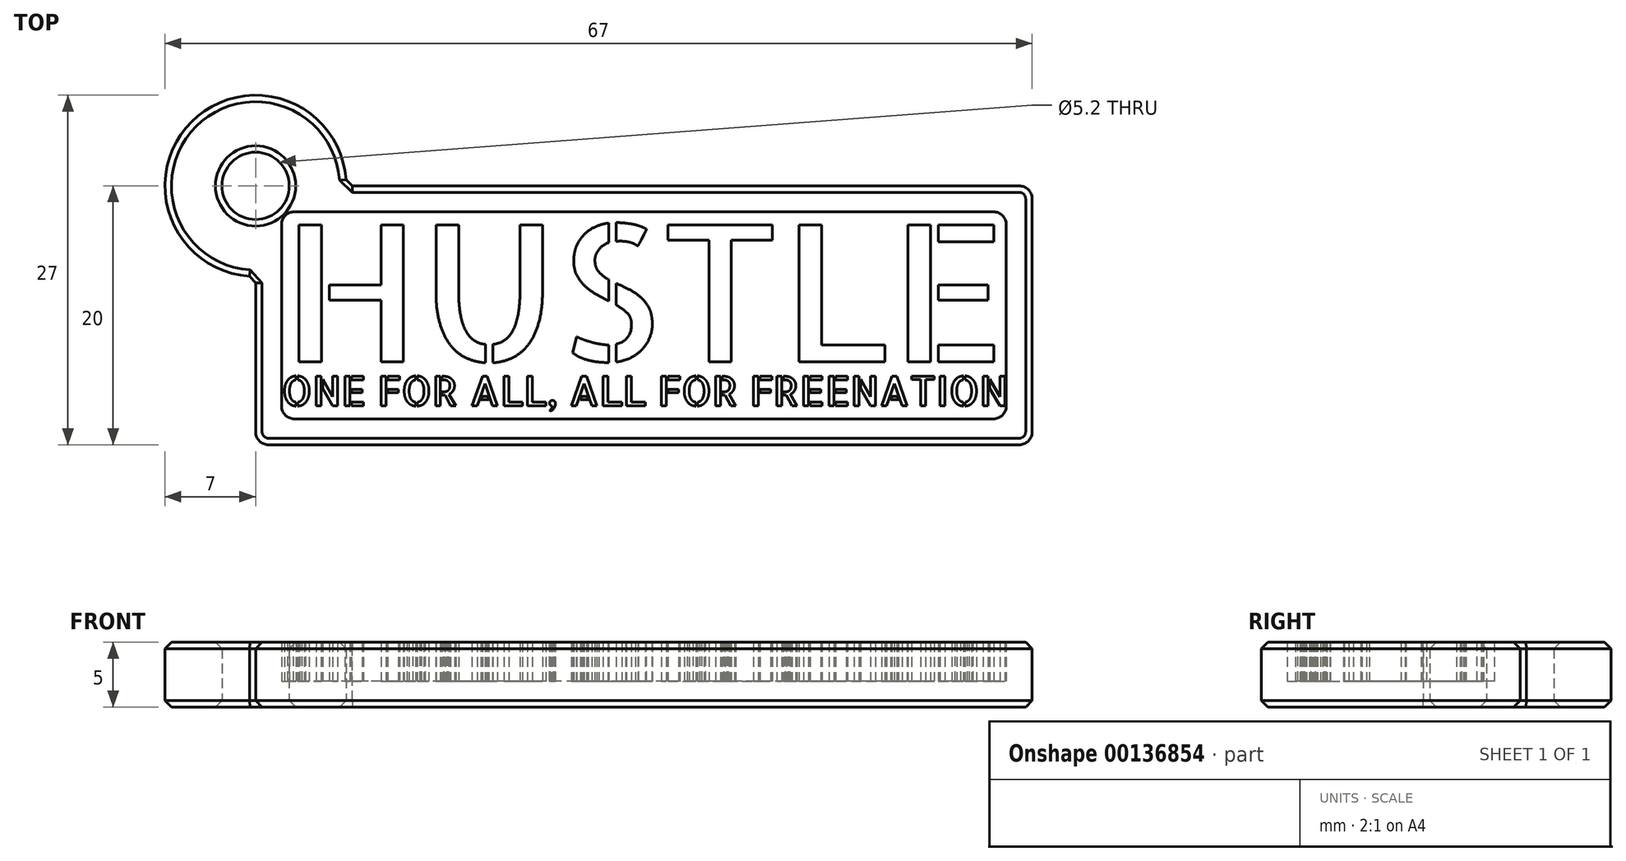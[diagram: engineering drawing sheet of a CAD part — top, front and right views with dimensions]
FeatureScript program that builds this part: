
annotation { "Feature Type Name" : "Feature", "Feature Type Description" : "" }
export const myFeature = defineFeature(function(context is Context, id is Id, definition is map)
    precondition{}
    {
        {
            var Q0;
            Q0=qCreatedBy(makeId("Top.planeOp"),FACE);
            var sketch = newSketch(context, id + "F0", { "sketchPlane" : qUnion([Q0])});
            skLineSegment(sketch, "E0.bottom", {"start": v(29, -10) * mm, "end": v(-29, -10) * mm});
            skLineSegment(sketch, "E0.top", {"start": v(29, 10) * mm, "end": v(-27.4, 10) * mm});
            skLineSegment(sketch, "E0.left", {"start": v(30, -9) * mm, "end": v(30, 9) * mm});
            skLineSegment(sketch, "E0.right", {"start": v(-30, -9) * mm, "end": v(-30, 7.4) * mm});
            skPoint(sketch, "E0.middle", {"position": v(0, 0) * mm});
            skLineSegment(sketch, "E1.0", {"start": v(27, 8) * mm, "end": v(-27, 8) * mm});
            skLineSegment(sketch, "E1.1", {"start": v(28, -7) * mm, "end": v(28, 7) * mm});
            skLineSegment(sketch, "E1.2", {"start": v(27, -8) * mm, "end": v(-27, -8) * mm});
            skLineSegment(sketch, "E1.3", {"start": v(-28, -7) * mm, "end": v(-28, 7) * mm});
            skArc(sketch, "E2", {"start": v(-23, 10) * mm, "mid": v(-34.95, 14.95) * mm, "end": v(-30, 3) * mm});
            skCircle(sketch, "E3.0", {"center": v(-30, 10) * mm, "radius": 2.6 * mm});
            skPoint(sketch, "E4.visualSharp", {"position": v(-30, -10) * mm});
            skArc(sketch, "E4.filletArc", {"start": v(-30, -9) * mm, "mid": v(-29.7, -9.7) * mm, "end": v(-29, -10) * mm});
            skPoint(sketch, "E5.visualSharp", {"position": v(30, -10) * mm});
            skArc(sketch, "E5.filletArc", {"start": v(29, -10) * mm, "mid": v(29.7, -9.7) * mm, "end": v(30, -9) * mm});
            skPoint(sketch, "E6.visualSharp", {"position": v(30, 10) * mm});
            skArc(sketch, "E6.filletArc", {"start": v(30, 9) * mm, "mid": v(29.7, 9.7) * mm, "end": v(29, 10) * mm});
            skPoint(sketch, "E7.visualSharp", {"position": v(28, 8) * mm});
            skArc(sketch, "E7.filletArc", {"start": v(28, 7) * mm, "mid": v(27.7, 7.7) * mm, "end": v(27, 8) * mm});
            skPoint(sketch, "E8.visualSharp", {"position": v(28, -8) * mm});
            skArc(sketch, "E8.filletArc", {"start": v(27, -8) * mm, "mid": v(27.7, -7.7) * mm, "end": v(28, -7) * mm});
            skPoint(sketch, "E9.visualSharp", {"position": v(-28, -8) * mm});
            skArc(sketch, "E9.filletArc", {"start": v(-28, -7) * mm, "mid": v(-27.7, -7.7) * mm, "end": v(-27, -8) * mm});
            skPoint(sketch, "E10.visualSharp", {"position": v(-28, 8) * mm});
            skArc(sketch, "E10.filletArc", {"start": v(-27, 8) * mm, "mid": v(-27.7, 7.7) * mm, "end": v(-28, 7) * mm});
            skSolve(sketch);
        }
        {
            var Q0;
            Q0=makeQuery(id+"F0.imprint","IMPRINT",FACE,{"disambiguationData":[TD([[makeQuery(id+"F0.imprint","IMPRINT",EDGE,{"derivedFrom":sQuery(id+"F0.wireOp",EDGE,"E0.bottom")}),-1.0]])]});
            var Q1;
            {var subQ3=sQuery(id+"F0.wireOp",EDGE,"E2");Q1=makeQuery(id+"F0.imprint","IMPRINT",FACE,{"disambiguationData":[TD([[makeQuery(id+"F0.imprint","IMPRINT",EDGE,{"derivedFrom":subQ3}),1.0]])]});}
            extrude(context, id + "F1", {"entities" : qUnion([Q0, Q1]), "depth" : 5 * mm});
        }
        {
            var Q0;
            Q0=makeQuery(id+"F0.imprint","IMPRINT",FACE,{"disambiguationData":[TD([[makeQuery(id+"F0.imprint","IMPRINT",EDGE,{"derivedFrom":sQuery(id+"F0.wireOp",EDGE,"E1.0")}),1.0]])]});
            extrude(context, id + "F2", {"entities" : qUnion([Q0]), "operationType" : NewBodyOperationType.ADD, "depth" : 2 * mm});
        }
        {
            var Q0;
            Q0=makeQuery(id+"F1.opExtrude","CAP_EDGE",EDGE,{"disambiguationData":[OSD([sQuery(id+"F0.wireOp",EDGE,"E0.right")])],"isStart":false});
            var Q1;
            Q1=makeQuery(id+"F1.opExtrude","CAP_EDGE",EDGE,{"disambiguationData":[OSD([sQuery(id+"F0.wireOp",EDGE,"E2")])],"isStart":false});
            var Q2;
            Q2=makeQuery(id+"F1.opExtrude","CAP_EDGE",EDGE,{"disambiguationData":[OSD([sQuery(id+"F0.wireOp",EDGE,"E0.right")])],"isStart":true});
            var Q3;
            Q3=makeQuery(id+"F1.opExtrude","CAP_EDGE",EDGE,{"disambiguationData":[OSD([sQuery(id+"F0.wireOp",EDGE,"E2")])],"isStart":true});
            var Q4;
            Q4=makeQuery(id+"F1.opExtrude","CAP_EDGE",EDGE,{"disambiguationData":[OSD([sQuery(id+"F0.wireOp",EDGE,"E3.0")])],"isStart":false});
            var Q5;
            Q5=makeQuery(id+"F1.opExtrude","CAP_EDGE",EDGE,{"disambiguationData":[OSD([sQuery(id+"F0.wireOp",EDGE,"E3.0")])],"isStart":true});
            var Q6;
            Q6=makeQuery(id+"F1.opExtrude","SWEPT_EDGE",EDGE,{"disambiguationData":[OSD([sQuery(id+"F0.wireOp",EDGE,"E0.right"),sQuery(id+"F0.wireOp",EDGE,"E2")])]});
            var Q7;
            Q7=makeQuery(id+"F1.opExtrude","SWEPT_EDGE",EDGE,{"disambiguationData":[OSD([sQuery(id+"F0.wireOp",EDGE,"E0.top"),sQuery(id+"F0.wireOp",EDGE,"E2")])]});
            chamfer(context, id + "F3", {"entities" : qUnion([Q0, Q1, Q2, Q3, Q4, Q5, Q6, Q7]), "width" : 0.5 * mm, "tangentPropagation" : true});
        }
        {
            var Q0;
            Q0=makeQuery(id+"F2.opExtrude","CAP_FACE",FACE,{"disambiguationData":[OSD([sQuery(id+"F0.wireOp",EDGE,"E1.0"),sQuery(id+"F0.wireOp",EDGE,"E1.1"),sQuery(id+"F0.wireOp",EDGE,"E1.2"),sQuery(id+"F0.wireOp",EDGE,"E1.3"),sQuery(id+"F0.wireOp",EDGE,"E7.filletArc"),sQuery(id+"F0.wireOp",EDGE,"E8.filletArc"),sQuery(id+"F0.wireOp",EDGE,"E9.filletArc"),sQuery(id+"F0.wireOp",EDGE,"E10.filletArc")])],"isStart":false});
            var sketch = newSketch(context, id + "F4", { "sketchPlane" : qUnion([Q0])});
            skText(sketch, "E11", { "text": "HUSTLE", "fontName": "AllertaStencil-Regular.ttf"});
            skText(sketch, "E12", { "text": "ONE FOR ALL, ALL FOR FREENATION", "fontName": "AllertaStencil-Regular.ttf"});
            const initialGuessF4  = {"E11": [-0.028, -0.00359, 1, 0, 0.01059], "E12": [-0.028, -0.007, 1, 0, 0.00229]};
            skSetInitialGuess(sketch, initialGuessF4);
            skSolve(sketch);
        }
        {
            var Q0;
            Q0 = qSketchRegion(id + "F4", true);
            var Q1;
            Q1=makeQuery(id+"F1.opExtrude","CAP_FACE",FACE,{"disambiguationData":[OSD([sQuery(id+"F0.wireOp",EDGE,"E0.bottom"),sQuery(id+"F0.wireOp",EDGE,"E0.top"),sQuery(id+"F0.wireOp",EDGE,"E0.left"),sQuery(id+"F0.wireOp",EDGE,"E0.right"),sQuery(id+"F0.wireOp",EDGE,"E1.0"),sQuery(id+"F0.wireOp",EDGE,"E1.1"),sQuery(id+"F0.wireOp",EDGE,"E1.2"),sQuery(id+"F0.wireOp",EDGE,"E1.3"),sQuery(id+"F0.wireOp",EDGE,"E2"),sQuery(id+"F0.wireOp",EDGE,"E3.0"),sQuery(id+"F0.wireOp",EDGE,"E4.filletArc"),sQuery(id+"F0.wireOp",EDGE,"E5.filletArc"),sQuery(id+"F0.wireOp",EDGE,"E6.filletArc"),sQuery(id+"F0.wireOp",EDGE,"E7.filletArc"),sQuery(id+"F0.wireOp",EDGE,"E8.filletArc"),sQuery(id+"F0.wireOp",EDGE,"E9.filletArc"),sQuery(id+"F0.wireOp",EDGE,"E10.filletArc")])],"isStart":false});
            extrude(context, id + "F5", {"entities" : qUnion([Q0]), "operationType" : NewBodyOperationType.ADD, "endBound" : BoundingType.UP_TO_SURFACE, "endBoundEntityFace" : qUnion([Q1]), "depth" : 25 * mm});
        }
    });
